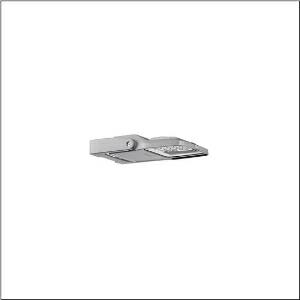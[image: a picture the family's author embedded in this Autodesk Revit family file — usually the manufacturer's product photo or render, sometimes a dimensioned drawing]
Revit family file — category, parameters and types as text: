
# Revit family: floodlight_fl_21_iq_micro___pl33t_5xa7762a4f2a_0497
name_source: partatom
category: Lighting Fixtures
units: mm (PartAtom-declared; Revit-internal decimal feet)

## family parameters
Cut with Voids When Loaded = No
Host = Face
Light Source = No
Part Type = Normal
Room Calculation Point = No
Round Connector Dimension = Use Diameter
Shared = No

## types (1)
- --- (1 x LED, 3050 lm, 23.1 W, 4000K)
    Apparent Load = 23 VA
    CIE Flux Codes = 26 75 99 100 100
    Color Rendering = 70
    Color Temperature = 4000K
    Default Elevation = 1800 mm
    Description = Floodlight FL 21 iQ micro, floodlight, primary light control with lens, of PMMA, primary optical cover: protective disc, of toughened safety glass, transparent, light distribution: PL33T, light emission: direct distribution, installation type: surface-mounted, lamps: LED, High Power LED, rated values: 3.050lm | 23,1W | 132lm/W (begin service life); end service life: 3.050lm | 23,8W; at 50% lumin. flux: 1.525lm | 11W | 138,6lm/W, colour temperature: 4000K, colour rendering: CRI > 70, light colour: 740, light setting 1 begin service life: 100% | 3.050lm | 23,1W | 132lm/W | 4.000K, light setting 1 end service life: 23,8W, further light settings possible, control: Auto-Match, Temp-Guard, Night-Set, Smart-Wire, Desk-Remote (wireless, voltage-free reading and setting of iQ features in the workshop via application-optimized NFC function/RFID function), optimised constant luminous flux control (CLO 2.0), Street-Remote, pre-setting: linear dimming characteristic, with terminal, 6-pole, mains connection: 220..240V, AC, 50/60Hz, luminaire housing, of diecast aluminium, powder-coated, SITECO metallic grey (DB 702S), corrosivity category C5 mid according to DIN EN ISO 12944suitable for swimming poolschlorine-resistant, sealing non-destructively replaceable, design bracket, of diecast aluminium, powder-coated, SITECO metallic grey (DB 702S), protection rating (complete): IP66, insulation class (complete): insulation class II (safety insulation), certification: CE, ENEC, VDE, protection symbol: D, impact resistance: IK07, permissible operating ambient temperature: -40..+40°C, permissible operating ambient temperature for outdoor applications: -40..+50°C, standard: DIN EN 12944, LABS conformity tested according to VDMA 24364:2018-05, packaging unit: 1 piece

Light Distribution: PL33T
    Height = 65 mm
    Lamp = 1 x LED
    Lamp Light Flux = 3050 lm
    Lamp Power = 23.1 W
    Lamp count = 1
    Length = 312 mm
    Luminous efficacy = 132 lm/W
    Manufacturer = Siteco
    ModVariant = No
    Model = 5XA7762A4F2A
    Mounting Place = Wall
    Mounting Type = Surface mounted
    Number of Poles = 1
    OnlyDefault = Yes
    Power Factor = 1
    Product Name = Floodlight FL 21 iQ micro | PL33T
    Product group = floodlight | wall mounted
    ProductGroupID = 2002
    Protection Class = Protection class II
    Protection Degree = IP 66
    RLX_Detail_Level = 1
    RLX_Emergency_Light_Flux = 0 lm
    RLX_Emergency_Type = 0
    RLX_Emergency_Type_DB = No
    RlxData = <blob elided: 97673 chars, md5=340c9f15>
    Socket = socket
    Standby Power = 0 W
    System Light Flux = 3050 lm
    System Power = 23 W
    Type Comments = factory setting: luminous flux: 100 % | dim-lin: 254 | 455 mA
    Type Image = l_1006878.jpg
    URL = http://relux.com
    VarID = @adj_147389
    Voltage = 0 V
    Weight = 0.00 kg
    Width = 230 mm

## geometry (parser evidence)
native form markers: Blend x4, Sweep x14
no freeform markers — native parametric forms only
